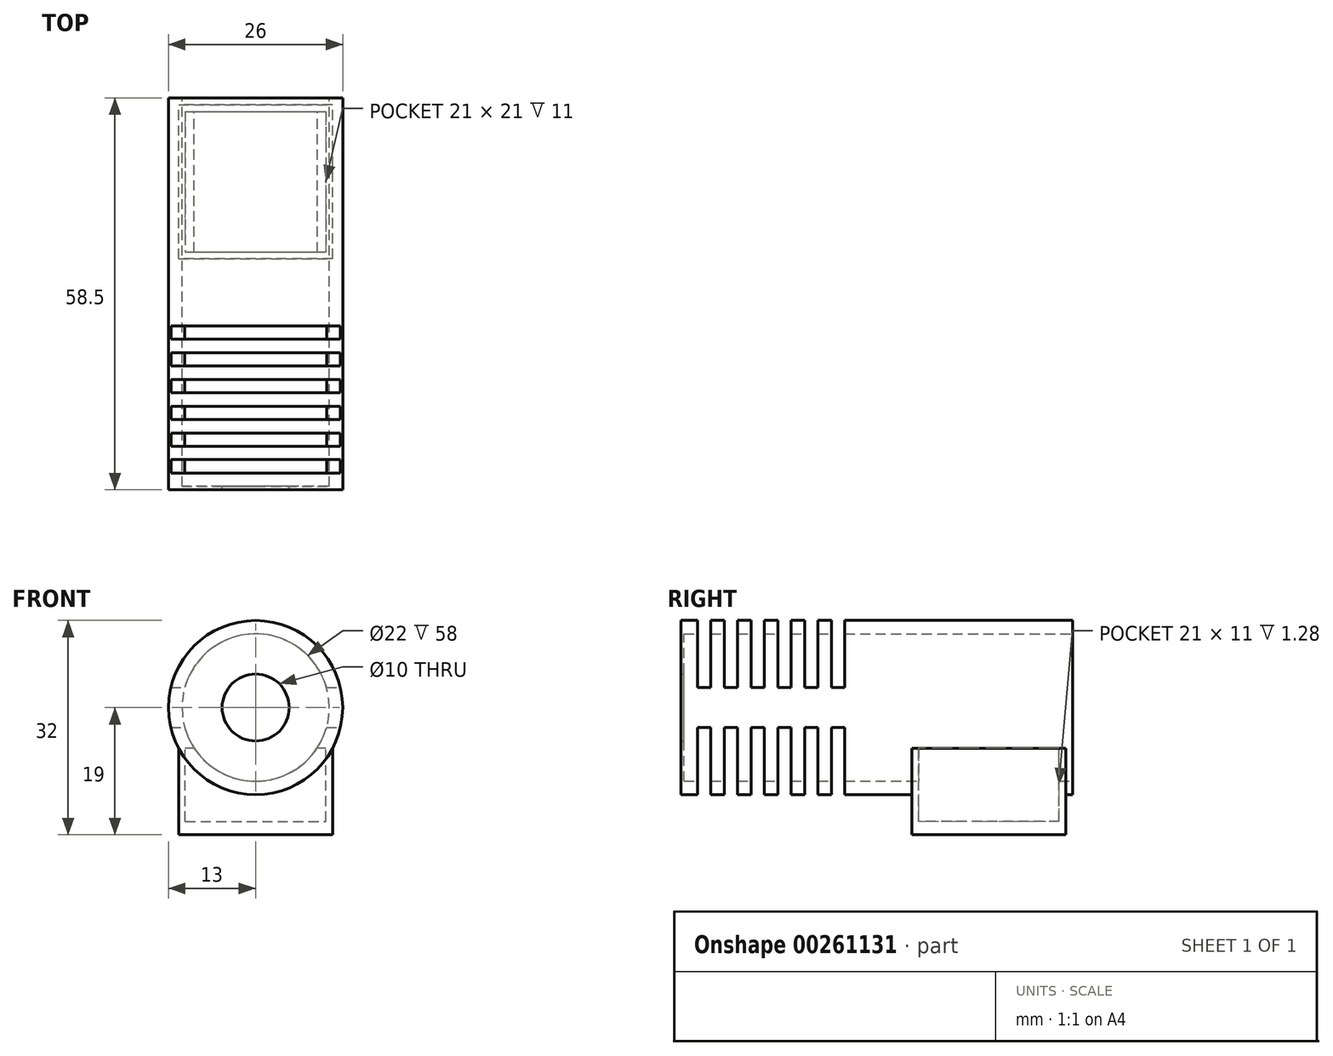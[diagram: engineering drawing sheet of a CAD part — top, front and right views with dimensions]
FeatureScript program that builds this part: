
annotation { "Feature Type Name" : "Feature", "Feature Type Description" : "" }
export const myFeature = defineFeature(function(context is Context, id is Id, definition is map)
    precondition{}
    {
        {
            var Q0;
            Q0=qCreatedBy(makeId("Front.planeOp"),FACE);
            var sketch = newSketch(context, id + "F0", { "sketchPlane" : qUnion([Q0])});
            skCircle(sketch, "E0", {"center": v(0, 0) * mm, "radius": 13 * mm});
            skCircle(sketch, "E1", {"center": v(0, 0) * mm, "radius": 11 * mm});
            skSolve(sketch);
        }
        {
            var Q0;
            Q0=qSketchRegion(id+"F0",true);
            extrude(context, id + "F1", {"entities" : qUnion([Q0]), "depth" : 58 * mm});
        }
        {
            var Q0;
            Q0=makeQuery(id+"F1.opExtrude","CAP_FACE",FACE,{"disambiguationData":[OSD([sQuery(id+"F0.wireOp",EDGE,"E0"),sQuery(id+"F0.wireOp",EDGE,"E1")])],"isStart":false});
            var sketch = newSketch(context, id + "F2", { "sketchPlane" : qUnion([Q0])});
            skCircle(sketch, "E2", {"center": v(0, 0) * mm, "radius": 13 * mm});
            skCircle(sketch, "E3", {"center": v(0, 0) * mm, "radius": 5 * mm});
            skSolve(sketch);
        }
        {
            var Q0;
            Q0=qSketchRegion(id+"F2",true);
            extrude(context, id + "F3", {"entities" : qUnion([Q0]), "operationType" : NewBodyOperationType.ADD, "depth" : 0.5 * mm});
        }
        {
            var Q0;
            Q0=qCreatedBy(makeId("Top.planeOp"),FACE);
            cPlane(context, id + "F4", {"entities" : qUnion([Q0]), "cplaneType" : CPlaneType.OFFSET, "offset" : 13 * mm, "width" : 150 * mm, "height" : 150 * mm});
        }
        {
            var Q0;
            Q0=qCreatedBy(id+"F4.planeOp",FACE);
            var sketch = newSketch(context, id + "F5", { "sketchPlane" : qUnion([Q0])});
            skLineSegment(sketch, "E4", {"start": v(0, 0) * mm, "end": v(0, -58) * mm});
            skLineSegment(sketch, "E5", {"start": v(-13, -58) * mm, "end": v(13, -58) * mm});
            skLineSegment(sketch, "E6", {"start": v(-13, -56) * mm, "end": v(-13, -54) * mm});
            skLineSegment(sketch, "E7", {"start": v(-13, -32) * mm, "end": v(13, -32) * mm});
            skLineSegment(sketch, "E8", {"start": v(13, -34) * mm, "end": v(13, -36) * mm});
            skLineSegment(sketch, "E9.0.1.0", {"start": v(-13, -56) * mm, "end": v(13, -56) * mm});
            skLineSegment(sketch, "E9.0.2.0", {"start": v(-13, -54) * mm, "end": v(13, -54) * mm});
            skLineSegment(sketch, "E9.0.3.0", {"start": v(-13, -52) * mm, "end": v(13, -52) * mm});
            skLineSegment(sketch, "E9.0.4.0", {"start": v(-13, -50) * mm, "end": v(13, -50) * mm});
            skLineSegment(sketch, "E9.0.5.0", {"start": v(-13, -48) * mm, "end": v(13, -48) * mm});
            skLineSegment(sketch, "E9.0.6.0", {"start": v(-13, -46) * mm, "end": v(13, -46) * mm});
            skLineSegment(sketch, "E9.0.7.0", {"start": v(-13, -44) * mm, "end": v(13, -44) * mm});
            skLineSegment(sketch, "E9.0.8.0", {"start": v(-13, -42) * mm, "end": v(13, -42) * mm});
            skLineSegment(sketch, "E9.0.9.0", {"start": v(-13, -40) * mm, "end": v(13, -40) * mm});
            skLineSegment(sketch, "E9.0.10.0", {"start": v(-13, -38) * mm, "end": v(13, -38) * mm});
            skLineSegment(sketch, "E9.0.11.0", {"start": v(-13, -36) * mm, "end": v(13, -36) * mm});
            skLineSegment(sketch, "E9.0.12.0", {"start": v(-13, -34) * mm, "end": v(13, -34) * mm});
            skLineSegment(sketch, "E10.trimOffspring", {"start": v(-13, -36) * mm, "end": v(-13, -34) * mm});
            skLineSegment(sketch, "E11.trimOffspring", {"start": v(13, -38) * mm, "end": v(13, -40) * mm});
            skLineSegment(sketch, "E12.trimOffspring", {"start": v(-13, -40) * mm, "end": v(-13, -38) * mm});
            skLineSegment(sketch, "E13.trimOffspring", {"start": v(13, -42) * mm, "end": v(13, -44) * mm});
            skLineSegment(sketch, "E14.trimOffspring", {"start": v(-13, -44) * mm, "end": v(-13, -42) * mm});
            skLineSegment(sketch, "E15.trimOffspring", {"start": v(13, -46) * mm, "end": v(13, -48) * mm});
            skLineSegment(sketch, "E16.trimOffspring", {"start": v(-13, -48) * mm, "end": v(-13, -46) * mm});
            skLineSegment(sketch, "E17.trimOffspring", {"start": v(13, -50) * mm, "end": v(13, -52) * mm});
            skLineSegment(sketch, "E18.trimOffspring", {"start": v(-13, -52) * mm, "end": v(-13, -50) * mm});
            skLineSegment(sketch, "E19.trimOffspring", {"start": v(13, -54) * mm, "end": v(13, -56) * mm});
            skLineSegment(sketch, "E20", {"start": v(0, 0) * mm, "end": v(0, -1) * mm});
            skSolve(sketch);
        }
        {
            var Q0;
            Q0=qSketchRegion(id+"F5",true);
            extrude(context, id + "F6", {"entities" : qUnion([Q0]), "operationType" : NewBodyOperationType.REMOVE, "oppositeDirection" : true, "depth" : 10 * mm});
        }
        {
            var Q0;
            Q0=qCreatedBy(makeId("Top.planeOp"),FACE);
            cPlane(context, id + "F7", {"entities" : qUnion([Q0]), "cplaneType" : CPlaneType.OFFSET, "offset" : 13 * mm, "oppositeDirection" : true, "width" : 150 * mm, "height" : 150 * mm});
        }
        {
            var Q0;
            Q0=qCreatedBy(id+"F7.planeOp",FACE);
            var sketch = newSketch(context, id + "F8", { "sketchPlane" : qUnion([Q0])});
            skLineSegment(sketch, "E21", {"start": v(0, 0) * mm, "end": v(0, -52) * mm});
            skLineSegment(sketch, "E22", {"start": v(13, -56) * mm, "end": v(13, -54) * mm});
            skLineSegment(sketch, "E23", {"start": v(-13, -56) * mm, "end": v(-13, -54) * mm});
            skLineSegment(sketch, "E24.0.1.0", {"start": v(-13, -56) * mm, "end": v(13, -56) * mm});
            skLineSegment(sketch, "E24.0.2.0", {"start": v(-13, -54) * mm, "end": v(13, -54) * mm});
            skLineSegment(sketch, "E24.0.3.0", {"start": v(-13, -52) * mm, "end": v(13, -52) * mm});
            skLineSegment(sketch, "E24.0.4.0", {"start": v(-13, -50) * mm, "end": v(13, -50) * mm});
            skLineSegment(sketch, "E24.0.5.0", {"start": v(-13, -48) * mm, "end": v(13, -48) * mm});
            skLineSegment(sketch, "E24.0.6.0", {"start": v(-13, -46) * mm, "end": v(13, -46) * mm});
            skLineSegment(sketch, "E24.0.7.0", {"start": v(-13, -44) * mm, "end": v(13, -44) * mm});
            skLineSegment(sketch, "E24.0.8.0", {"start": v(-13, -42) * mm, "end": v(13, -42) * mm});
            skLineSegment(sketch, "E24.0.9.0", {"start": v(-13, -40) * mm, "end": v(13, -40) * mm});
            skLineSegment(sketch, "E24.0.10.0", {"start": v(-13, -38) * mm, "end": v(13, -38) * mm});
            skLineSegment(sketch, "E24.0.11.0", {"start": v(-13, -36) * mm, "end": v(13, -36) * mm});
            skLineSegment(sketch, "E24.0.12.0", {"start": v(-13, -34) * mm, "end": v(13, -34) * mm});
            skLineSegment(sketch, "E25.trimOffspring", {"start": v(-13, -52) * mm, "end": v(-13, -50) * mm});
            skLineSegment(sketch, "E26.trimOffspring", {"start": v(13, -52) * mm, "end": v(13, -50) * mm});
            skLineSegment(sketch, "E27.trimOffspring", {"start": v(-13, -54) * mm, "end": v(-13, -56) * mm});
            skLineSegment(sketch, "E28.trimOffspring", {"start": v(-13, -50) * mm, "end": v(-13, -52) * mm});
            skLineSegment(sketch, "E29.trimOffspring", {"start": v(-13, -48) * mm, "end": v(-13, -46) * mm});
            skLineSegment(sketch, "E30.trimOffspring", {"start": v(13, -48) * mm, "end": v(13, -46) * mm});
            skLineSegment(sketch, "E31.trimOffspring", {"start": v(-13, -46) * mm, "end": v(-13, -48) * mm});
            skLineSegment(sketch, "E32.trimOffspring", {"start": v(-13, -44) * mm, "end": v(-13, -42) * mm});
            skLineSegment(sketch, "E33.trimOffspring", {"start": v(13, -44) * mm, "end": v(13, -42) * mm});
            skLineSegment(sketch, "E34.trimOffspring", {"start": v(-13, -42) * mm, "end": v(-13, -44) * mm});
            skLineSegment(sketch, "E35.trimOffspring", {"start": v(13, -40) * mm, "end": v(13, -38) * mm});
            skLineSegment(sketch, "E36.trimOffspring", {"start": v(-13, -38) * mm, "end": v(-13, -40) * mm});
            skLineSegment(sketch, "E37.trimOffspring", {"start": v(-13, -36) * mm, "end": v(-13, -34) * mm});
            skLineSegment(sketch, "E38.trimOffspring", {"start": v(13, -36) * mm, "end": v(13, -34) * mm});
            skLineSegment(sketch, "E39.trimOffspring", {"start": v(-13, -34) * mm, "end": v(-13, -36) * mm});
            skSolve(sketch);
        }
        {
            var Q0;
            Q0=qSketchRegion(id+"F8",true);
            extrude(context, id + "F9", {"entities" : qUnion([Q0]), "operationType" : NewBodyOperationType.REMOVE, "depth" : 10 * mm});
        }
        {
            var Q0;
            Q0=qCreatedBy(makeId("Top.planeOp"),FACE);
            cPlane(context, id + "F10", {"entities" : qUnion([Q0]), "cplaneType" : CPlaneType.OFFSET, "offset" : 6 * mm, "oppositeDirection" : true, "width" : 150 * mm, "height" : 150 * mm});
        }
        {
            var Q0;
            Q0=qCreatedBy(id+"F10.planeOp",FACE);
            var sketch = newSketch(context, id + "F11", { "sketchPlane" : qUnion([Q0])});
            skLineSegment(sketch, "E40", {"start": v(0, 0) * mm, "end": v(0, -1) * mm});
            skLineSegment(sketch, "E41", {"start": v(0, -1) * mm, "end": v(-11.5, -1) * mm});
            skLineSegment(sketch, "E42", {"start": v(-11.5, -1) * mm, "end": v(11.5, -1) * mm});
            skLineSegment(sketch, "E43.top", {"start": v(-11.5, -24) * mm, "end": v(11.5, -24) * mm});
            skLineSegment(sketch, "E43.left", {"start": v(-11.5, -1) * mm, "end": v(-11.5, -24) * mm});
            skLineSegment(sketch, "E43.right", {"start": v(11.5, -1) * mm, "end": v(11.5, -24) * mm});
            skPoint(sketch, "E44.orphan", {"position": v(-13, -1) * mm});
            skSolve(sketch);
        }
        {
            var Q0;
            Q0 = qSketchRegion(id + "F11", true);
            extrude(context, id + "F12", {"entities" : qUnion([Q0]), "operationType" : NewBodyOperationType.REMOVE, "oppositeDirection" : true, "depth" : 25 * mm});
        }
        {
            var Q0;
            Q0=qCreatedBy(id+"F10.planeOp",FACE);
            var sketch = newSketch(context, id + "F13", { "sketchPlane" : qUnion([Q0])});
            skLineSegment(sketch, "E45", {"start": v(0, 0) * mm, "end": v(0, -1) * mm});
            skLineSegment(sketch, "E46", {"start": v(0, -1) * mm, "end": v(-11.5, -1) * mm});
            skLineSegment(sketch, "E47", {"start": v(-11.5, -1) * mm, "end": v(11.5, -1) * mm});
            skLineSegment(sketch, "E48", {"start": v(11.5, -1) * mm, "end": v(11.5, -24) * mm});
            skLineSegment(sketch, "E49", {"start": v(11.5, -24) * mm, "end": v(-11.5, -24) * mm});
            skLineSegment(sketch, "E50", {"start": v(-11.5, -24) * mm, "end": v(-11.5, -1) * mm});
            skLineSegment(sketch, "E51.bottom", {"start": v(-10.5, -2) * mm, "end": v(10.5, -2) * mm});
            skLineSegment(sketch, "E51.top", {"start": v(-10.5, -23) * mm, "end": v(10.5, -23) * mm});
            skLineSegment(sketch, "E51.left", {"start": v(-10.5, -2) * mm, "end": v(-10.5, -23) * mm});
            skLineSegment(sketch, "E51.right", {"start": v(10.5, -2) * mm, "end": v(10.5, -23) * mm});
            skSolve(sketch);
        }
        {
            var Q0;
            {var subQ0=sQuery(id+"F13.wireOp",EDGE,"E48");Q0=makeQuery(id+"F13.imprint","IMPRINT",FACE,{"disambiguationData":[TD([[makeQuery(id+"F13.imprint","IMPRINT",EDGE,{"derivedFrom":subQ0}),-1.0]])]});}
            extrude(context, id + "F14", {"entities" : qUnion([Q0]), "operationType" : NewBodyOperationType.ADD, "oppositeDirection" : true, "depth" : 11 * mm});
        }
        {
            var Q0;
            Q0=qCreatedBy(makeId("Front.planeOp"),FACE);
            var sketch = newSketch(context, id + "F15", { "sketchPlane" : qUnion([Q0])});
            skCircle(sketch, "E52", {"center": v(0, 0) * mm, "radius": 11 * mm});
            skSolve(sketch);
        }
        {
            var Q0;
            Q0 = qSketchRegion(id + "F15", true);
            extrude(context, id + "F16", {"entities" : qUnion([Q0]), "operationType" : NewBodyOperationType.REMOVE, "depth" : 58 * mm});
        }
        {
            var Q0;
            Q0=makeQuery(id+"F14.opExtrude","CAP_FACE",FACE,{"disambiguationData":[OSD([sQuery(id+"F13.wireOp",EDGE,"E47"),sQuery(id+"F13.wireOp",EDGE,"E48"),sQuery(id+"F13.wireOp",EDGE,"E49"),sQuery(id+"F13.wireOp",EDGE,"E50"),sQuery(id+"F13.wireOp",EDGE,"E51.bottom"),sQuery(id+"F13.wireOp",EDGE,"E51.top"),sQuery(id+"F13.wireOp",EDGE,"E51.left"),sQuery(id+"F13.wireOp",EDGE,"E51.right")])],"isStart":false});
            var sketch = newSketch(context, id + "F17", { "sketchPlane" : qUnion([Q0])});
            skLineSegment(sketch, "E53", {"start": v(0, 0) * mm, "end": v(0, 1) * mm});
            skLineSegment(sketch, "E54.bottom", {"start": v(-11.5, 1) * mm, "end": v(11.5, 1) * mm});
            skLineSegment(sketch, "E54.top", {"start": v(-11.5, 24) * mm, "end": v(11.5, 24) * mm});
            skLineSegment(sketch, "E54.left", {"start": v(-11.5, 1) * mm, "end": v(-11.5, 24) * mm});
            skLineSegment(sketch, "E54.right", {"start": v(11.5, 1) * mm, "end": v(11.5, 24) * mm});
            skSolve(sketch);
        }
        {
            var Q0;
            Q0 = qSketchRegion(id + "F17", true);
            extrude(context, id + "F18", {"entities" : qUnion([Q0]), "operationType" : NewBodyOperationType.ADD, "depth" : 2 * mm});
        }
    });
